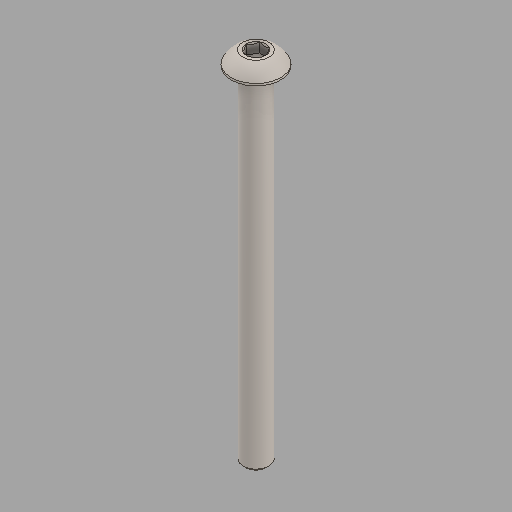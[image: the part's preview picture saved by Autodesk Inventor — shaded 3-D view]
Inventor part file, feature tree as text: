
AUTODESK INVENTOR PART (.ipt)
format: ipt  version: 2024.2 (Build 282272000, 272)  size: 107,008 bytes
history: native  units: in
note: dims shown in document units (in); Inventor stores cm internally (conversion verified against a paired STEP export)
features: fillet x1
ambient origin geometry x8: Origin, YZ Plane, XZ Plane, XY Plane, X Axis, Y Axis, Z Axis, Center Point
bodies: Solid1 (feature_tree)
feature tree (1):
  fillet  "Fillet1"  [1 undecoded]
note: 1 required parameter value undecoded (feature->parameter linkage not recoverable at this tier; creation-order binding heuristic only, values carry confidence <= 0.55)
